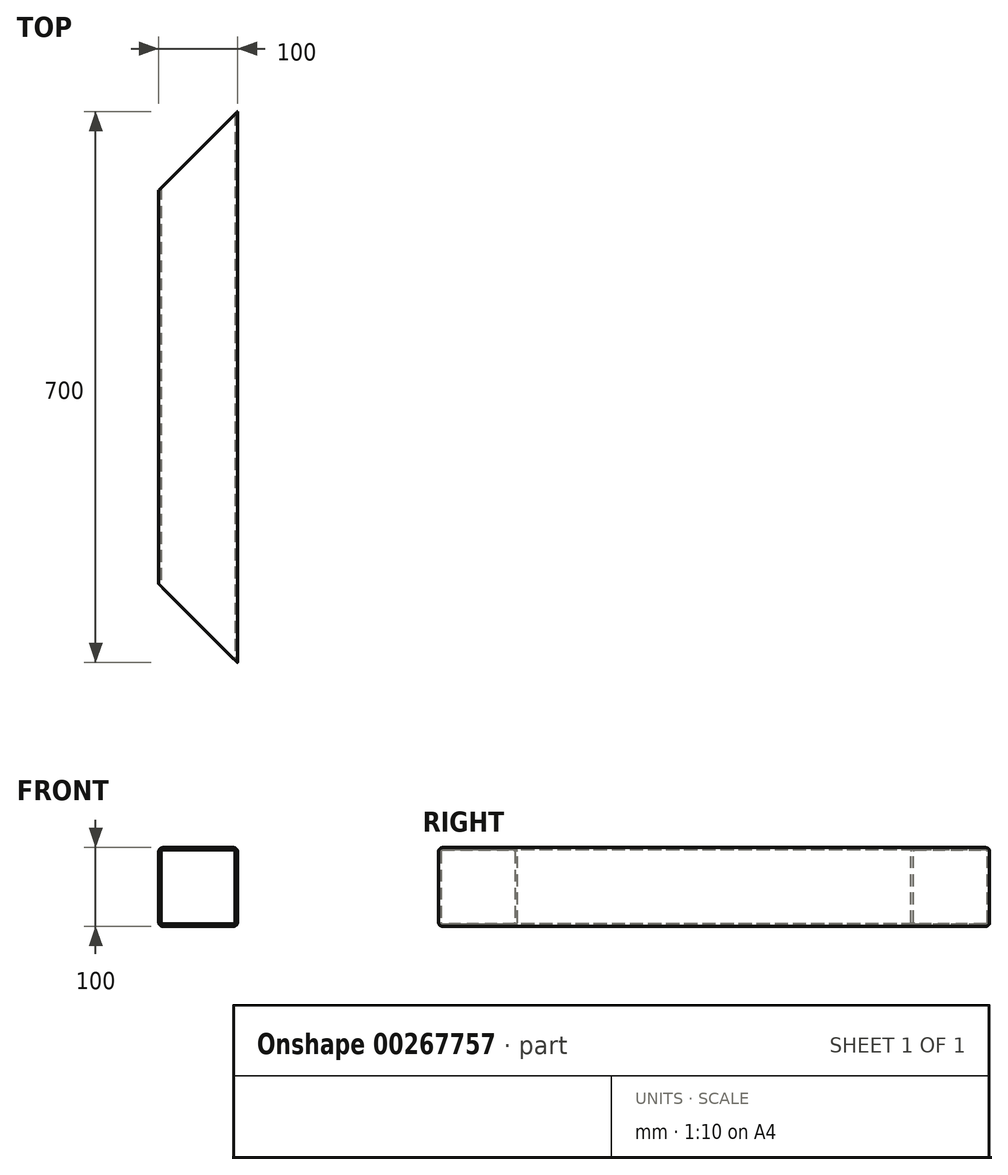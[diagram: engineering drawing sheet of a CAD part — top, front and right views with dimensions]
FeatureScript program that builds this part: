
annotation { "Feature Type Name" : "Feature", "Feature Type Description" : "" }
export const myFeature = defineFeature(function(context is Context, id is Id, definition is map)
    precondition{}
    {
        {
            var Q0;
            Q0=qCreatedBy(makeId("Front.planeOp"),FACE);
            var sketch = newSketch(context, id + "F0", { "sketchPlane" : qUnion([Q0])});
            skLineSegment(sketch, "E0.bottom", {"start": v(45, 50) * mm, "end": v(-45, 50) * mm});
            skLineSegment(sketch, "E0.top", {"start": v(45, -50) * mm, "end": v(-45, -50) * mm});
            skLineSegment(sketch, "E0.left", {"start": v(50, 45) * mm, "end": v(50, -45) * mm});
            skLineSegment(sketch, "E0.right", {"start": v(-50, 45) * mm, "end": v(-50, -45) * mm});
            skPoint(sketch, "E0.middle", {"position": v(0, 0) * mm});
            skPoint(sketch, "E1.visualSharp", {"position": v(-50, 50) * mm});
            skArc(sketch, "E1.filletArc", {"start": v(-45, 50) * mm, "mid": v(-48.54, 48.54) * mm, "end": v(-50, 45) * mm});
            skPoint(sketch, "E2.visualSharp", {"position": v(50, 50) * mm});
            skArc(sketch, "E2.filletArc", {"start": v(50, 45) * mm, "mid": v(48.54, 48.54) * mm, "end": v(45, 50) * mm});
            skPoint(sketch, "E3.visualSharp", {"position": v(50, -50) * mm});
            skArc(sketch, "E3.filletArc", {"start": v(45, -50) * mm, "mid": v(48.54, -48.54) * mm, "end": v(50, -45) * mm});
            skPoint(sketch, "E4.visualSharp", {"position": v(-50, -50) * mm});
            skArc(sketch, "E4.filletArc", {"start": v(-50, -45) * mm, "mid": v(-48.54, -48.54) * mm, "end": v(-45, -50) * mm});
            skArc(sketch, "E5.0", {"start": v(-45, 47) * mm, "mid": v(-46.41, 46.41) * mm, "end": v(-47, 45) * mm});
            skLineSegment(sketch, "E5.1", {"start": v(45, 47) * mm, "end": v(-45, 47) * mm});
            skLineSegment(sketch, "E5.2", {"start": v(-47, 45) * mm, "end": v(-47, -45) * mm});
            skArc(sketch, "E5.3", {"start": v(47, 45) * mm, "mid": v(46.41, 46.41) * mm, "end": v(45, 47) * mm});
            skArc(sketch, "E5.4", {"start": v(-47, -45) * mm, "mid": v(-46.41, -46.41) * mm, "end": v(-45, -47) * mm});
            skLineSegment(sketch, "E5.5", {"start": v(45, -47) * mm, "end": v(-45, -47) * mm});
            skArc(sketch, "E5.6", {"start": v(45, -47) * mm, "mid": v(46.41, -46.41) * mm, "end": v(47, -45) * mm});
            skLineSegment(sketch, "E5.7", {"start": v(47, 45) * mm, "end": v(47, -45) * mm});
            skSolve(sketch);
        }
        {
            var Q0;
            Q0=makeQuery(id+"F0.imprint","IMPRINT",FACE,{"disambiguationData":[TD([[makeQuery(id+"F0.imprint","IMPRINT",EDGE,{"derivedFrom":sQuery(id+"F0.wireOp",EDGE,"E0.bottom")}),1.0]])]});
            extrude(context, id + "F1", {"entities" : qUnion([Q0]), "oppositeDirection" : true, "depth" : 700 * mm});
        }
        {
            var Q0;
            Q0=makeQuery(id+"F1.opExtrude","SWEPT_FACE",FACE,{"disambiguationData":[OSD([sQuery(id+"F0.wireOp",EDGE,"E0.bottom")])]});
            cPlane(context, id + "F2", {"entities" : qUnion([Q0]), "cplaneType" : CPlaneType.OFFSET, "offset" : 0 * mm, "width" : 150 * mm, "height" : 150 * mm});
        }
        {
            var Q0;
            Q0=qCreatedBy(id+"F2.planeOp",FACE);
            var sketch = newSketch(context, id + "F3", { "sketchPlane" : qUnion([Q0])});
            skLineSegment(sketch, "E6.bottom", {"start": v(-50, 0) * mm, "end": v(50, 0) * mm});
            skLineSegment(sketch, "E6.top", {"start": v(-50, 100) * mm, "end": v(50, 100) * mm, "construction": true});
            skLineSegment(sketch, "E6.left", {"start": v(-50, 0) * mm, "end": v(-50, 100) * mm});
            skLineSegment(sketch, "E6.right", {"start": v(50, 0) * mm, "end": v(50, 100) * mm, "construction": true});
            skLineSegment(sketch, "E7", {"start": v(50, 0) * mm, "end": v(-50, 100) * mm});
            skLineSegment(sketch, "E8.bottom", {"start": v(-50, 700) * mm, "end": v(50, 700) * mm});
            skLineSegment(sketch, "E8.top", {"start": v(-50, 600) * mm, "end": v(50, 600) * mm, "construction": true});
            skLineSegment(sketch, "E8.left", {"start": v(-50, 700) * mm, "end": v(-50, 600) * mm});
            skLineSegment(sketch, "E8.right", {"start": v(50, 700) * mm, "end": v(50, 600) * mm, "construction": true});
            skLineSegment(sketch, "E9", {"start": v(-50, 600) * mm, "end": v(50, 700) * mm});
            skSolve(sketch);
        }
        {
            var Q0;
            Q0=makeQuery(id+"F3.imprint","IMPRINT",FACE,{"disambiguationData":[TD([[makeQuery(id+"F3.imprint","IMPRINT",EDGE,{"derivedFrom":sQuery(id+"F3.wireOp",EDGE,"E6.bottom")}),1.0]])]});
            extrude(context, id + "F4", {"entities" : qUnion([Q0]), "operationType" : NewBodyOperationType.REMOVE, "endBound" : BoundingType.THROUGH_ALL, "oppositeDirection" : true, "depth" : 25 * mm});
        }
        {
            var Q0;
            Q0 = qSketchRegion(id + "F3", true);
            extrude(context, id + "F5", {"entities" : qUnion([Q0]), "operationType" : NewBodyOperationType.REMOVE, "endBound" : BoundingType.THROUGH_ALL, "oppositeDirection" : true, "depth" : 25 * mm});
        }
    });
